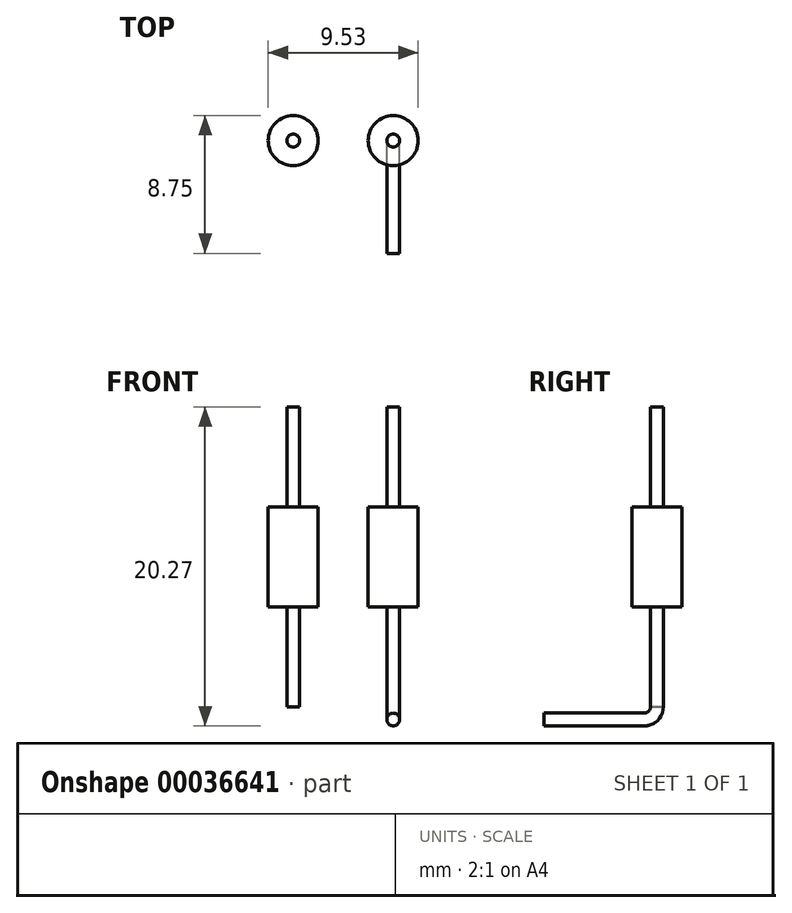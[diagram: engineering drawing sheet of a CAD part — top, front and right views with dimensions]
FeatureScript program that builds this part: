
annotation { "Feature Type Name" : "Feature", "Feature Type Description" : "" }
export const myFeature = defineFeature(function(context is Context, id is Id, definition is map)
    precondition{}
    {
        {
            var Q0;
            Q0=qCreatedBy(makeId("Top.planeOp"),FACE);
            var sketch = newSketch(context, id + "F0", { "sketchPlane" : qUnion([Q0])});
            skCircle(sketch, "E0", {"center": v(0, 0) * mm, "radius": 1.59 * mm});
            skCircle(sketch, "E1", {"center": v(0, 0) * mm, "radius": 0.4 * mm});
            skSolve(sketch);
        }
        {
            var Q0;
            Q0=makeQuery(id+"F0.imprint","IMPRINT",FACE,{"disambiguationData":[TD([[makeQuery(id+"F0.imprint","IMPRINT",EDGE,{"derivedFrom":sQuery(id+"F0.wireOp",EDGE,"E0")}),1.0]])]});
            var Q1;
            Q1=makeQuery(id+"F0.imprint","IMPRINT",FACE,{"disambiguationData":[TD([[makeQuery(id+"F0.imprint","IMPRINT",EDGE,{"derivedFrom":sQuery(id+"F0.wireOp",EDGE,"E1")}),1.0]])]});
            extrude(context, id + "F1", {"entities" : qUnion([Q0, Q1]), "depth" : 6.35 * mm});
        }
        {
            var Q0;
            Q0=makeQuery(id+"F0.imprint","IMPRINT",FACE,{"disambiguationData":[TD([[makeQuery(id+"F0.imprint","IMPRINT",EDGE,{"derivedFrom":sQuery(id+"F0.wireOp",EDGE,"E1")}),1.0]])]});
            extrude(context, id + "F2", {"entities" : qUnion([Q0]), "operationType" : NewBodyOperationType.ADD, "oppositeDirection" : true, "depth" : 6.35 * mm});
        }
        {
            var Q0;
            Q0=makeQuery(id+"F0.imprint","IMPRINT",FACE,{"disambiguationData":[TD([[makeQuery(id+"F0.imprint","IMPRINT",EDGE,{"derivedFrom":sQuery(id+"F0.wireOp",EDGE,"E1")}),1.0]])]});
            extrude(context, id + "F3", {"entities" : qUnion([Q0]), "operationType" : NewBodyOperationType.ADD, "depth" : 12.7 * mm});
        }
        {
            var Q0;
            Q0=makeQuery(id+"F1.opExtrude","SWEPT_BODY",BODY,{"disambiguationData":[OSD([sQuery(id+"F0.wireOp",EDGE,"E0")])]});
            transform(context, id + "F4", {"entities" : qUnion([Q0]), "transformType" : TransformType.TRANSLATION_3D, "dx" : -6.35 * mm, "dy" : 0 * mm, "dz" : 0 * mm, "makeCopy" : true});
        }
        {
            var Q0;
            Q0=qCreatedBy(makeId("Right.planeOp"),FACE);
            var sketch = newSketch(context, id + "F5", { "sketchPlane" : qUnion([Q0])});
            skLineSegment(sketch, "E2", {"start": v(-0.4, -6.35) * mm, "end": v(0, -6.35) * mm});
            skCircle(sketch, "E3", {"center": v(-0.81, -6.35) * mm, "radius": 0.4 * mm});
            skSolve(sketch);
        }
        {
            var Q0;
            Q0=makeQuery(id+"F2.opExtrude","CAP_FACE",FACE,{"disambiguationData":[OSD([sQuery(id+"F0.wireOp",EDGE,"E1")])],"isStart":false});
            var Q1;
            Q1=sQuery(id+"F5.wireOp",EDGE,"E3");
            revolve(context, id + "F6", {"operationType" : NewBodyOperationType.ADD, "entities" : qUnion([Q0]), "axis" : qUnion([Q1]), "revolveType" : RevolveType.ONE_DIRECTION, "oppositeDirection" : true, "angle" : 90 * degree});
        }
        {
            var Q0;
            Q0=makeQuery(id+"F6.opRevolve","CAP_FACE",FACE,{"disambiguationData":[OSD([sQuery(id+"F0.wireOp",EDGE,"E1")])],"isStart":false});
            extrude(context, id + "F7", {"entities" : qUnion([Q0]), "operationType" : NewBodyOperationType.ADD, "depth" : 6.35 * mm});
        }
    });
